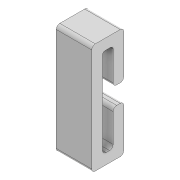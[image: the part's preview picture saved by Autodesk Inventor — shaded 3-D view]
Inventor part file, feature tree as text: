
AUTODESK INVENTOR PART (.ipt)
format: ipt  version: 2020 (Build 240168000, 168)  size: 247,296 bytes
history: native  units: mm
features: other x1, extrude x1, sketch x1
ambient origin geometry x8: Origin, YZ Plane, XZ Plane, XY Plane, X Axis, Y Axis, Z Axis, Center Point
bodies: Body1 (feature_tree)
feature tree (3):
  other  "Твердое тело1"
  extrude  "Выдавливание1"  Depth=3.0mm
  sketch  "Эскиз1"
